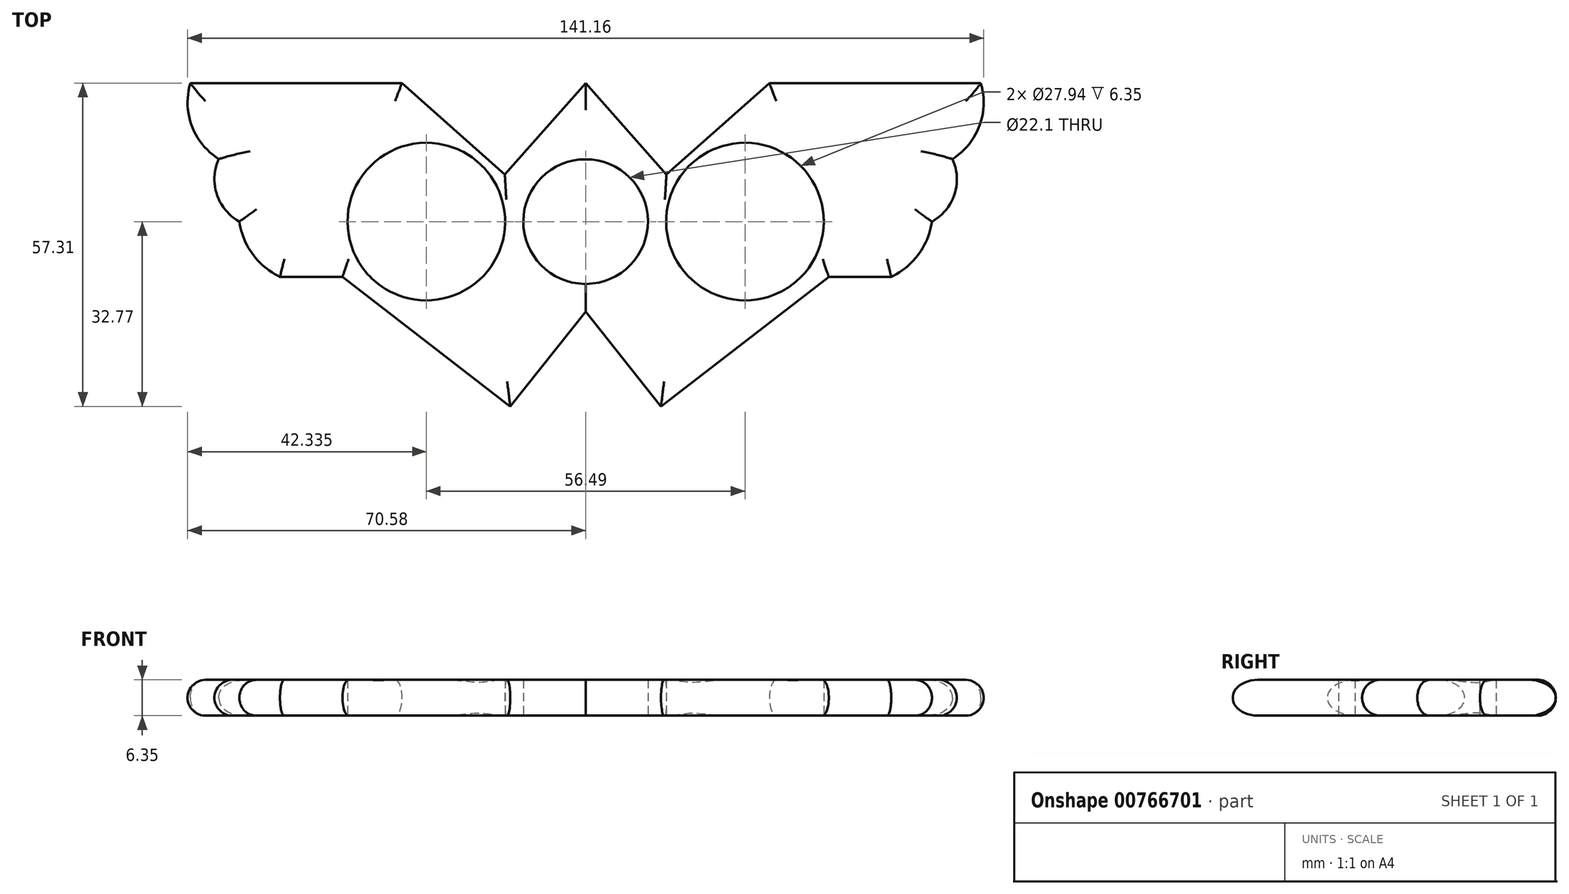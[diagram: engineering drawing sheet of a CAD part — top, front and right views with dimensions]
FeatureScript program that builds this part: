
annotation { "Feature Type Name" : "Feature", "Feature Type Description" : "" }
export const myFeature = defineFeature(function(context is Context, id is Id, definition is map)
    precondition{}
    {
        {
            var Q0;
            Q0=qCreatedBy(makeId("Top.planeOp"),FACE);
            var sketch = newSketch(context, id + "F0", { "sketchPlane" : qUnion([Q0])});
            skCircle(sketch, "E0", {"center": v(0, 0) * mm, "radius": 11.05 * mm});
            skCircle(sketch, "E1", {"center": v(-28.24, 0) * mm, "radius": 11.05 * mm});
            skLineSegment(sketch, "E2", {"start": v(0, 24.54) * mm, "end": v(-14.33, 8.37) * mm});
            skLineSegment(sketch, "E3", {"start": v(-14.33, 8.37) * mm, "end": v(-32.58, 24.54) * mm});
            skLineSegment(sketch, "E4", {"start": v(-32.58, 24.54) * mm, "end": v(-56.32, 24.54) * mm});
            skLineSegment(sketch, "E5.MirrorCS", {"start": v(0, 24.54) * mm, "end": v(14.33, 8.37) * mm});
            skLineSegment(sketch, "E6.MirrorCS", {"start": v(32.58, 24.54) * mm, "end": v(56.32, 24.54) * mm});
            skLineSegment(sketch, "E7.MirrorCS", {"start": v(14.33, 8.37) * mm, "end": v(32.58, 24.54) * mm});
            skCircle(sketch, "E8.MirrorC", {"center": v(28.24, 0) * mm, "radius": 11.05 * mm});
            skLineSegment(sketch, "E9.1.0.1", {"start": v(-14.14, -13.63) * mm, "end": v(-18.37, -9.88) * mm});
            skLineSegment(sketch, "E9.1.0.3", {"start": v(8.6, -6.95) * mm, "end": v(14.51, -13.63) * mm});
            skLineSegment(sketch, "E9.1.0.4", {"start": v(14.51, -13.63) * mm, "end": v(18.55, -10.06) * mm});
            skPoint(sketch, "E10.orphan", {"position": v(32.77, 2.54) * mm});
            skLineSegment(sketch, "E11", {"start": v(39.4, 8.41) * mm, "end": v(42.4, 11.07) * mm});
            skLineSegment(sketch, "E12", {"start": v(42.4, 11.07) * mm, "end": v(51.59, 11.08) * mm});
            skCircle(sketch, "E13", {"center": v(28.24, 0) * mm, "radius": 13.97 * mm});
            skCircle(sketch, "E14", {"center": v(-28.24, 0) * mm, "radius": 13.97 * mm});
            skLineSegment(sketch, "E15", {"start": v(42.21, 0) * mm, "end": v(51.59, 0) * mm});
            skLineSegment(sketch, "E16", {"start": v(51.59, 11.08) * mm, "end": v(51.59, 11.08) * mm});
            skLineSegment(sketch, "E17", {"start": v(56.32, 24.54) * mm, "end": v(70.09, 24.54) * mm});
            skLineSegment(sketch, "E18", {"start": v(51.59, 11.08) * mm, "end": v(65.04, 11.1) * mm});
            skArc(sketch, "E19", {"start": v(65.04, 11.1) * mm, "mid": v(69.82, 16.97) * mm, "end": v(70.09, 24.54) * mm});
            skArc(sketch, "E20", {"start": v(61.4, 0) * mm, "mid": v(65.39, 4.84) * mm, "end": v(65.04, 11.1) * mm});
            skLineSegment(sketch, "E21.MirrorCS", {"start": v(-39.4, 8.41) * mm, "end": v(-42.4, 11.07) * mm});
            skLineSegment(sketch, "E22.MirrorCS", {"start": v(-42.4, 11.07) * mm, "end": v(-51.59, 11.08) * mm});
            skLineSegment(sketch, "E23.MirrorCS", {"start": v(-51.59, 11.08) * mm, "end": v(-51.59, 11.08) * mm});
            skLineSegment(sketch, "E24.MirrorCS", {"start": v(-51.59, 11.08) * mm, "end": v(-65.04, 11.1) * mm});
            skLineSegment(sketch, "E25.MirrorCS", {"start": v(-56.32, 24.54) * mm, "end": v(-70.09, 24.54) * mm});
            skArc(sketch, "E26.MirrorCS", {"start": v(-65.04, 11.1) * mm, "mid": v(-69.82, 16.97) * mm, "end": v(-70.09, 24.54) * mm});
            skArc(sketch, "E27.MirrorCS", {"start": v(-61.4, 0) * mm, "mid": v(-65.39, 4.84) * mm, "end": v(-65.04, 11.1) * mm});
            skLineSegment(sketch, "E28.1.0.0", {"start": v(0, -15.96) * mm, "end": v(-13.37, -32.77) * mm});
            skLineSegment(sketch, "E28.1.0.3", {"start": v(-43.11, -9.81) * mm, "end": v(-54.19, -9.81) * mm});
            skLineSegment(sketch, "E28.1.0.4", {"start": v(-52.8, -9.4) * mm, "end": v(-54.19, -9.81) * mm});
            skLineSegment(sketch, "E29", {"start": v(51.59, 0) * mm, "end": v(61.4, 0) * mm});
            skLineSegment(sketch, "E30.MirrorCS", {"start": v(-51.59, 0) * mm, "end": v(-61.4, 0) * mm});
            skLineSegment(sketch, "E31.MirrorCS", {"start": v(-42.21, 0) * mm, "end": v(-51.59, 0) * mm});
            skArc(sketch, "E32.MirrorCS", {"start": v(-54.19, -9.81) * mm, "mid": v(-59.02, -5.8) * mm, "end": v(-61.4, 0) * mm});
            skPoint(sketch, "E33.orphan", {"position": v(58.34, -6.26) * mm});
            skPoint(sketch, "E34.orphan", {"position": v(-65.12, -13.12) * mm});
            skLineSegment(sketch, "E35.trimOffspring", {"start": v(-8.41, -7.16) * mm, "end": v(-14.14, -13.63) * mm});
            skPoint(sketch, "E36.orphan", {"position": v(0.19, 2.54) * mm});
            skPoint(sketch, "E37.orphan", {"position": v(-32.77, 2.54) * mm});
            skPoint(sketch, "E38.orphan", {"position": v(-32.4, 2.54) * mm});
            skLineSegment(sketch, "E39.trimOffspring", {"start": v(-56.16, 0) * mm, "end": v(-56.13, 2.54) * mm, "construction": true});
            skLineSegment(sketch, "E40", {"start": v(-61.4, 0) * mm, "end": v(-42.21, 0) * mm});
            skLineSegment(sketch, "E41", {"start": v(42.21, 0) * mm, "end": v(61.4, 0) * mm});
            skPoint(sketch, "E28.1.0.7.end.orphan", {"position": v(59.36, -13.37) * mm});
            skPoint(sketch, "E28.1.0.8.start.orphan", {"position": v(50.04, -13.37) * mm});
            skPoint(sketch, "E42.start.orphan", {"position": v(54.19, -9.81) * mm});
            skLineSegment(sketch, "E43.MirrorCS", {"start": v(0, -15.96) * mm, "end": v(13.37, -32.77) * mm});
            skLineSegment(sketch, "E44.MirrorCS", {"start": v(43.11, -9.81) * mm, "end": v(54.19, -9.81) * mm});
            skArc(sketch, "E45.MirrorCS", {"start": v(54.19, -9.81) * mm, "mid": v(59.02, -5.8) * mm, "end": v(61.4, 0) * mm});
            skPoint(sketch, "E28.1.0.2.start.orphan", {"position": v(-27.1, -21.7) * mm});
            skPoint(sketch, "E28.1.0.1.end.orphan", {"position": v(-27.42, -21.7) * mm});
            skPoint(sketch, "E46.MirrorCS.end.orphan", {"position": v(27.42, -21.7) * mm});
            skPoint(sketch, "E46.MirrorCS.start.orphan", {"position": v(13.37, -32.77) * mm});
            skPoint(sketch, "E47.MirrorCS.end.orphan", {"position": v(43.11, -9.81) * mm});
            skPoint(sketch, "E47.MirrorCS.start.orphan", {"position": v(27.1, -21.7) * mm});
            skLineSegment(sketch, "E48", {"start": v(-43.11, -9.81) * mm, "end": v(-13.37, -32.77) * mm});
            skLineSegment(sketch, "E49.MirrorCS", {"start": v(43.11, -9.81) * mm, "end": v(13.37, -32.77) * mm});
            skSolve(sketch);
        }
        {
            var Q0;
            Q0=qSketchRegion(id+"F0",true);
            extrude(context, id + "F1", {"entities" : qUnion([Q0]), "depth" : 6.35 * mm, "offsetDistance" : 25.4 * mm});
        }
        {
            var Q0;
            Q0=makeQuery(id+"F1.opExtrude","CAP_EDGE",EDGE,{"disambiguationData":[OSD([sQuery(id+"F0.wireOp",EDGE,"E4"),sQuery(id+"F0.wireOp",EDGE,"E25.MirrorCS")])],"isStart":false});
            var Q1;
            Q1=makeQuery(id+"F1.opExtrude","CAP_EDGE",EDGE,{"disambiguationData":[OSD([sQuery(id+"F0.wireOp",EDGE,"E27.MirrorCS")])],"isStart":false});
            var Q2;
            Q2=makeQuery(id+"F1.opExtrude","CAP_EDGE",EDGE,{"disambiguationData":[OSD([sQuery(id+"F0.wireOp",EDGE,"E32.MirrorCS")])],"isStart":false});
            var Q3;
            Q3=makeQuery(id+"F1.opExtrude","CAP_EDGE",EDGE,{"disambiguationData":[OSD([sQuery(id+"F0.wireOp",EDGE,"E28.1.0.3")])],"isStart":false});
            var Q4;
            Q4=makeQuery(id+"F1.opExtrude","CAP_EDGE",EDGE,{"disambiguationData":[OSD([sQuery(id+"F0.wireOp",EDGE,"E48")])],"isStart":false});
            var Q5;
            Q5=makeQuery(id+"F1.opExtrude","CAP_EDGE",EDGE,{"disambiguationData":[OSD([sQuery(id+"F0.wireOp",EDGE,"E28.1.0.0")])],"isStart":false});
            var Q6;
            Q6=makeQuery(id+"F1.opExtrude","CAP_EDGE",EDGE,{"disambiguationData":[OSD([sQuery(id+"F0.wireOp",EDGE,"E43.MirrorCS")])],"isStart":false});
            var Q7;
            Q7=makeQuery(id+"F1.opExtrude","CAP_EDGE",EDGE,{"disambiguationData":[OSD([sQuery(id+"F0.wireOp",EDGE,"E49.MirrorCS")])],"isStart":false});
            var Q8;
            Q8=makeQuery(id+"F1.opExtrude","CAP_EDGE",EDGE,{"disambiguationData":[OSD([sQuery(id+"F0.wireOp",EDGE,"E44.MirrorCS")])],"isStart":false});
            var Q9;
            Q9=makeQuery(id+"F1.opExtrude","CAP_EDGE",EDGE,{"disambiguationData":[OSD([sQuery(id+"F0.wireOp",EDGE,"E45.MirrorCS")])],"isStart":false});
            var Q10;
            Q10=makeQuery(id+"F1.opExtrude","CAP_EDGE",EDGE,{"disambiguationData":[OSD([sQuery(id+"F0.wireOp",EDGE,"E3")])],"isStart":false});
            var Q11;
            Q11=makeQuery(id+"F1.opExtrude","CAP_EDGE",EDGE,{"disambiguationData":[OSD([sQuery(id+"F0.wireOp",EDGE,"E2")])],"isStart":false});
            var Q12;
            Q12=makeQuery(id+"F1.opExtrude","CAP_EDGE",EDGE,{"disambiguationData":[OSD([sQuery(id+"F0.wireOp",EDGE,"E5.MirrorCS")])],"isStart":false});
            var Q13;
            Q13=makeQuery(id+"F1.opExtrude","CAP_EDGE",EDGE,{"disambiguationData":[OSD([sQuery(id+"F0.wireOp",EDGE,"E7.MirrorCS")])],"isStart":false});
            var Q14;
            Q14=makeQuery(id+"F1.opExtrude","CAP_EDGE",EDGE,{"disambiguationData":[OSD([sQuery(id+"F0.wireOp",EDGE,"E6.MirrorCS"),sQuery(id+"F0.wireOp",EDGE,"E17")])],"isStart":false});
            var Q15;
            Q15=makeQuery(id+"F1.opExtrude","CAP_EDGE",EDGE,{"disambiguationData":[OSD([sQuery(id+"F0.wireOp",EDGE,"E19")])],"isStart":false});
            var Q16;
            Q16=makeQuery(id+"F1.opExtrude","CAP_EDGE",EDGE,{"disambiguationData":[OSD([sQuery(id+"F0.wireOp",EDGE,"E6.MirrorCS"),sQuery(id+"F0.wireOp",EDGE,"E17")])],"isStart":true});
            var Q17;
            Q17=makeQuery(id+"F1.opExtrude","CAP_EDGE",EDGE,{"disambiguationData":[OSD([sQuery(id+"F0.wireOp",EDGE,"E7.MirrorCS")])],"isStart":true});
            var Q18;
            Q18=makeQuery(id+"F1.opExtrude","CAP_EDGE",EDGE,{"disambiguationData":[OSD([sQuery(id+"F0.wireOp",EDGE,"E26.MirrorCS")])],"isStart":true});
            var Q19;
            Q19=makeQuery(id+"F1.opExtrude","CAP_EDGE",EDGE,{"disambiguationData":[OSD([sQuery(id+"F0.wireOp",EDGE,"E32.MirrorCS")])],"isStart":true});
            var Q20;
            Q20=makeQuery(id+"F1.opExtrude","CAP_EDGE",EDGE,{"disambiguationData":[OSD([sQuery(id+"F0.wireOp",EDGE,"E28.1.0.3")])],"isStart":true});
            var Q21;
            Q21=makeQuery(id+"F1.opExtrude","CAP_EDGE",EDGE,{"disambiguationData":[OSD([sQuery(id+"F0.wireOp",EDGE,"E48")])],"isStart":true});
            var Q22;
            Q22=makeQuery(id+"F1.opExtrude","CAP_EDGE",EDGE,{"disambiguationData":[OSD([sQuery(id+"F0.wireOp",EDGE,"E28.1.0.0")])],"isStart":true});
            var Q23;
            Q23=makeQuery(id+"F1.opExtrude","CAP_EDGE",EDGE,{"disambiguationData":[OSD([sQuery(id+"F0.wireOp",EDGE,"E43.MirrorCS")])],"isStart":true});
            var Q24;
            Q24=makeQuery(id+"F1.opExtrude","CAP_EDGE",EDGE,{"disambiguationData":[OSD([sQuery(id+"F0.wireOp",EDGE,"E19")])],"isStart":true});
            var Q25;
            Q25=makeQuery(id+"F1.opExtrude","CAP_EDGE",EDGE,{"disambiguationData":[OSD([sQuery(id+"F0.wireOp",EDGE,"E49.MirrorCS")])],"isStart":true});
            var Q26;
            Q26=makeQuery(id+"F1.opExtrude","CAP_EDGE",EDGE,{"disambiguationData":[OSD([sQuery(id+"F0.wireOp",EDGE,"E44.MirrorCS")])],"isStart":true});
            var Q27;
            Q27=makeQuery(id+"F1.opExtrude","CAP_EDGE",EDGE,{"disambiguationData":[OSD([sQuery(id+"F0.wireOp",EDGE,"E45.MirrorCS")])],"isStart":true});
            var Q28;
            Q28=makeQuery(id+"F1.opExtrude","CAP_EDGE",EDGE,{"disambiguationData":[OSD([sQuery(id+"F0.wireOp",EDGE,"E20")])],"isStart":false});
            var Q29;
            Q29=makeQuery(id+"F1.opExtrude","CAP_EDGE",EDGE,{"disambiguationData":[OSD([sQuery(id+"F0.wireOp",EDGE,"E20")])],"isStart":true});
            var Q30;
            Q30=makeQuery(id+"F1.opExtrude","CAP_EDGE",EDGE,{"disambiguationData":[OSD([sQuery(id+"F0.wireOp",EDGE,"E2")])],"isStart":true});
            var Q31;
            Q31=makeQuery(id+"F1.opExtrude","CAP_EDGE",EDGE,{"disambiguationData":[OSD([sQuery(id+"F0.wireOp",EDGE,"E5.MirrorCS")])],"isStart":true});
            var Q32;
            Q32=makeQuery(id+"F1.opExtrude","CAP_EDGE",EDGE,{"disambiguationData":[OSD([sQuery(id+"F0.wireOp",EDGE,"E3")])],"isStart":true});
            var Q33;
            Q33=makeQuery(id+"F1.opExtrude","CAP_EDGE",EDGE,{"disambiguationData":[OSD([sQuery(id+"F0.wireOp",EDGE,"E4"),sQuery(id+"F0.wireOp",EDGE,"E25.MirrorCS")])],"isStart":true});
            var Q34;
            Q34=makeQuery(id+"F1.opExtrude","CAP_EDGE",EDGE,{"disambiguationData":[OSD([sQuery(id+"F0.wireOp",EDGE,"E27.MirrorCS")])],"isStart":true});
            var Q35;
            Q35=makeQuery(id+"F1.opExtrude","CAP_EDGE",EDGE,{"disambiguationData":[OSD([sQuery(id+"F0.wireOp",EDGE,"E26.MirrorCS")])],"isStart":false});
            fillet(context, id + "F2", {"entities" : qUnion([Q0, Q1, Q2, Q3, Q4, Q5, Q6, Q7, Q8, Q9, Q10, Q11, Q12, Q13, Q14, Q15, Q16, Q17, Q18, Q19, Q20, Q21, Q22, Q23, Q24, Q25, Q26, Q27, Q28, Q29, Q30, Q31, Q32, Q33, Q34, Q35]), "radius" : 3.17 * mm, "tangentPropagation" : true, "allowEdgeOverflow" : false});
        }
    });
